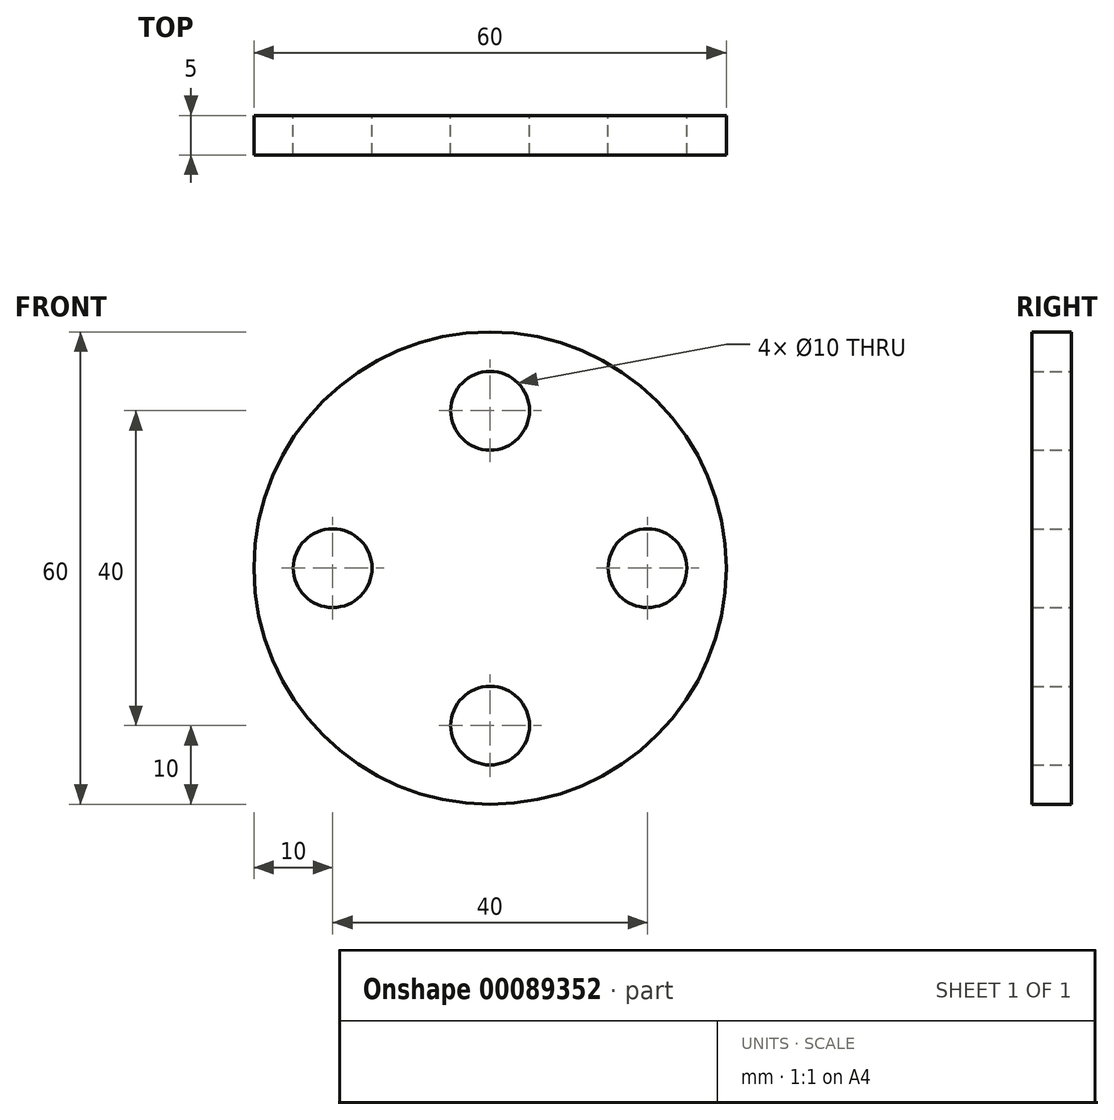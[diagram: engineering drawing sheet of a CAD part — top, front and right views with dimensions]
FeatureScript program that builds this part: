
annotation { "Feature Type Name" : "Feature", "Feature Type Description" : "" }
export const myFeature = defineFeature(function(context is Context, id is Id, definition is map)
    precondition{}
    {
        {
            var Q0;
            Q0=qCreatedBy(makeId("Front.planeOp"),FACE);
            var sketch = newSketch(context, id + "F0", { "sketchPlane" : qUnion([Q0])});
            skCircle(sketch, "E0", {"center": v(0, 0) * mm, "radius": 20 * mm, "construction": true});
            skCircle(sketch, "E1", {"center": v(0, 0) * mm, "radius": 30 * mm});
            skLineSegment(sketch, "E2", {"start": v(0, 51.25) * mm, "end": v(0, -48.67) * mm, "construction": true});
            skLineSegment(sketch, "E3", {"start": v(-50.53, 0) * mm, "end": v(59.72, 0) * mm, "construction": true});
            skCircle(sketch, "E4", {"center": v(0, -20) * mm, "radius": 5 * mm});
            skCircle(sketch, "E5", {"center": v(20, 0) * mm, "radius": 5 * mm});
            skCircle(sketch, "E6", {"center": v(-20, 0) * mm, "radius": 5 * mm});
            skCircle(sketch, "E7", {"center": v(0, 20) * mm, "radius": 5 * mm});
            skSolve(sketch);
        }
        {
            var Q0;
            Q0 = qSketchRegion(id + "F0", true);
            extrude(context, id + "F1", {"entities" : qUnion([Q0]), "depth" : 5 * mm});
        }
    });
